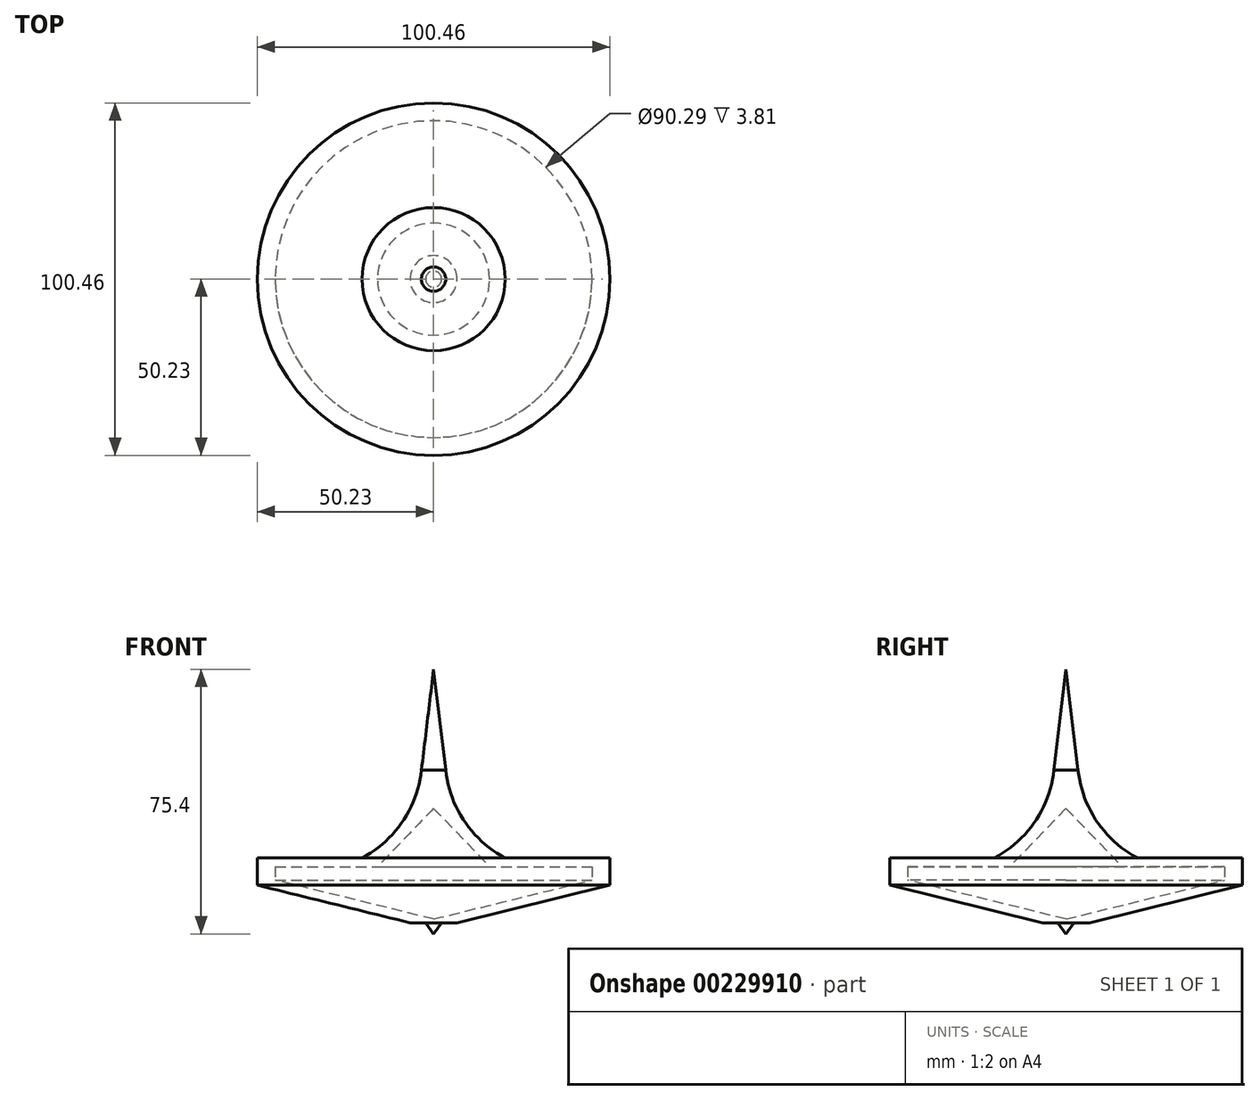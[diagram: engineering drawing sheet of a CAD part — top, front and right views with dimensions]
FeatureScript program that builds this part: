
annotation { "Feature Type Name" : "Feature", "Feature Type Description" : "" }
export const myFeature = defineFeature(function(context is Context, id is Id, definition is map)
    precondition{}
    {
        {
            var Q0;
            Q0=qCreatedBy(makeId("Front.planeOp"),FACE);
            var sketch = newSketch(context, id + "F0", { "sketchPlane" : qUnion([Q0])});
            skLineSegment(sketch, "E0", {"start": v(6.69, 9.26) * mm, "end": v(50.23, 19.97) * mm});
            skLineSegment(sketch, "E1", {"start": v(50.23, 19.97) * mm, "end": v(50.23, 27.81) * mm});
            skLineSegment(sketch, "E2", {"start": v(50.23, 27.81) * mm, "end": v(20.38, 27.81) * mm});
            skArc(sketch, "E3", {"start": v(20.38, 27.81) * mm, "mid": v(8.79, 38.2) * mm, "end": v(3.46, 52.81) * mm});
            skLineSegment(sketch, "E4", {"start": v(0, 53.75) * mm, "end": v(0, 81.5) * mm});
            skLineSegment(sketch, "E5", {"start": v(0, 81.5) * mm, "end": v(3.46, 52.81) * mm});
            skLineSegment(sketch, "E6", {"start": v(0, 10.36) * mm, "end": v(45.15, 21.46) * mm});
            skLineSegment(sketch, "E7", {"start": v(45.15, 21.46) * mm, "end": v(45.15, 25.27) * mm});
            skLineSegment(sketch, "E8", {"start": v(45.15, 25.27) * mm, "end": v(15.96, 25.27) * mm});
            skLineSegment(sketch, "E9", {"start": v(15.96, 25.27) * mm, "end": v(0, 41.88) * mm});
            skLineSegment(sketch, "E10.trimOffspring", {"start": v(0, 41.88) * mm, "end": v(0, 53.75) * mm});
            skLineSegment(sketch, "E11", {"start": v(6.69, 9.26) * mm, "end": v(2.28, 9.26) * mm});
            skLineSegment(sketch, "E12", {"start": v(0, 10.36) * mm, "end": v(0, 6.11) * mm});
            skLineSegment(sketch, "E13", {"start": v(2.28, 9.26) * mm, "end": v(0, 6.11) * mm});
            skSolve(sketch);
        }
        {
            var Q0;
            Q0=makeQuery(id+"F0.imprint","IMPRINT",FACE,{"disambiguationData":[TD([[makeQuery(id+"F0.imprint","IMPRINT",EDGE,{"derivedFrom":sQuery(id+"F0.wireOp",EDGE,"E0")}),1.0]])]});
            var Q1;
            Q1=sQuery(id+"F0.wireOp",EDGE,"E10.trimOffspring");
            revolve(context, id + "F1", {"entities" : qUnion([Q0]), "axis" : qUnion([Q1]), "revolveType" : RevolveType.FULL});
        }
    });
